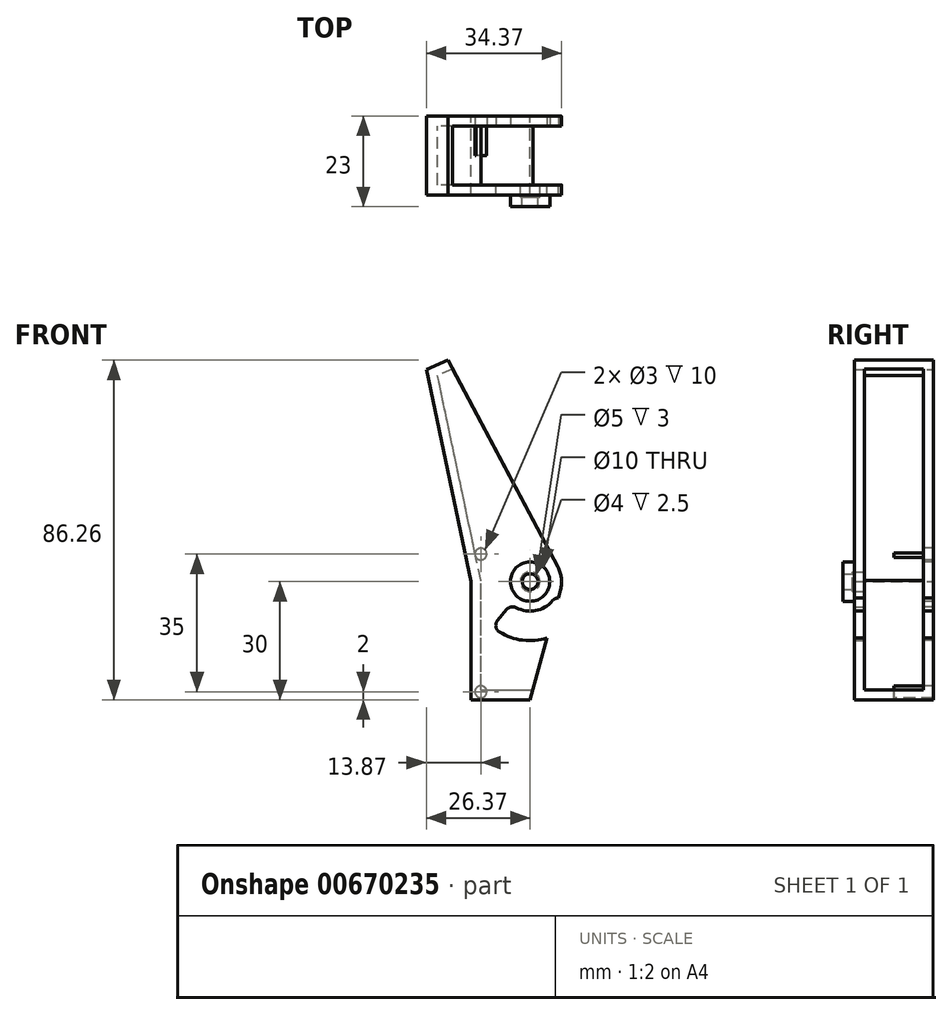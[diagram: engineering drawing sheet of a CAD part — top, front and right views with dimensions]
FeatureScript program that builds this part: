
annotation { "Feature Type Name" : "Feature", "Feature Type Description" : "" }
export const myFeature = defineFeature(function(context is Context, id is Id, definition is map)
    precondition{}
    {
        {
            var Q0;
            Q0=qCreatedBy(makeId("Front.planeOp"),FACE);
            var sketch = newSketch(context, id + "F0", { "sketchPlane" : qUnion([Q0])});
            skCircle(sketch, "E0", {"center": v(0, 0) * mm, "radius": 5 * mm});
            skSolve(sketch);
        }
        {
            var Q0;
            Q0=makeQuery(id+"F0.imprint","IMPRINT",FACE,{"disambiguationData":[TD([[makeQuery(id+"F0.imprint","IMPRINT",EDGE,{"derivedFrom":sQuery(id+"F0.wireOp",EDGE,"E0")}),1.0]])]});
            extrude(context, id + "F1", {"entities" : qUnion([Q0]), "depth" : 13 * mm, "offsetDistance" : 25 * mm});
        }
        {
            var Q0;
            Q0=qCreatedBy(makeId("Front.planeOp"),FACE);
            var sketch = newSketch(context, id + "F2", { "sketchPlane" : qUnion([Q0])});
            skLineSegment(sketch, "E1", {"start": v(7.06, 3.76) * mm, "end": v(-20.85, 56.26) * mm});
            skLineSegment(sketch, "E2", {"start": v(-20.85, 56.26) * mm, "end": v(-26.37, 53.9) * mm});
            skCircle(sketch, "E3", {"center": v(0, 0) * mm, "radius": 8 * mm});
            skCircle(sketch, "E4", {"center": v(0, 0) * mm, "radius": 60 * mm, "construction": true});
            skCircle(sketch, "E5", {"center": v(0, 0) * mm, "radius": 15 * mm, "construction": true});
            skLineSegment(sketch, "E6", {"start": v(-15, -30) * mm, "end": v(-15, 0) * mm});
            skLineSegment(sketch, "E7", {"start": v(-15, 0) * mm, "end": v(-26.37, 53.9) * mm});
            skLineSegment(sketch, "E8", {"start": v(0, -30) * mm, "end": v(7.71, -2.13) * mm});
            skLineSegment(sketch, "E9", {"start": v(-15, -30) * mm, "end": v(0, -30) * mm});
            skSolve(sketch);
        }
        {
            var Q0;
            {var subQ0=sQuery(id+"F2.wireOp",EDGE,"E2");Q0=makeQuery(id+"F2.imprint","IMPRINT",FACE,{"disambiguationData":[TD([[makeQuery(id+"F2.imprint","IMPRINT",EDGE,{"derivedFrom":subQ0}),1.0]])]});}
            var Q1;
            {var subQ0=sQuery(id+"F2.wireOp",EDGE,"E3");var subQ1=makeQuery(id+"F2.imprint","INTERSECT",VERTEX,{"derivedFrom":[sQuery(id+"F2.wireOp",EDGE,"ykASYGtx-wOTi-sknp-hqeL-7vM9FwBQ6DHq"),subQ0]});Q1=makeQuery(id+"F2.imprint","IMPRINT",FACE,{"disambiguationData":[TD([[makeQuery(id+"F2.imprint","IMPRINT",EDGE,{"disambiguationData":[TD([[subQ1,-1.0]])],"derivedFrom":subQ0}),1.0]])]});}
            var Q2;
            {var subQ4=sQuery(id+"F2.wireOp",EDGE,"AyMhzdsm-QS8C-DFPa-ot7w-gAMzFox847Q3");Q2=makeQuery(id+"F2.imprint","IMPRINT",FACE,{"disambiguationData":[TD([[makeQuery(id+"F2.imprint","IMPRINT",EDGE,{"derivedFrom":subQ4}),1.0]])]});}
            extrude(context, id + "F3", {"entities" : qUnion([Q0, Q1, Q2]), "operationType" : NewBodyOperationType.ADD, "endBound" : BoundingType.SYMMETRIC, "depth" : 20 * mm, "offsetDistance" : 25 * mm});
        }
        {
            var Q0;
            Q0=makeQuery(id+"F3.opExtrude","SWEPT_FACE",FACE,{"disambiguationData":[OSD([sQuery(id+"F2.wireOp",EDGE,"ykASYGtx-wOTi-sknp-hqeL-7vM9FwBQ6DHq")])]});
            var Q1;
            Q1=makeQuery(id+"F3.opExtrude","SWEPT_FACE",FACE,{"disambiguationData":[OSD([sQuery(id+"F2.wireOp",EDGE,"E3")])]});
            var Q2;
            Q2=makeQuery(id+"F3.opExtrude","SWEPT_FACE",FACE,{"disambiguationData":[OSD([sQuery(id+"F2.wireOp",EDGE,"E1")])]});
            var Q3;
            Q3=makeQuery(id+"F3.opExtrude","SWEPT_FACE",FACE,{"disambiguationData":[OSD([sQuery(id+"F2.wireOp",EDGE,"aPccT8il-h5co-UbTb-6sFN-h3AVFNnhd7PD")])]});
            var Q4;
            Q4=makeQuery(id+"F3.opExtrude","SWEPT_FACE",FACE,{"disambiguationData":[OSD([sQuery(id+"F2.wireOp",EDGE,"E8")])]});
            shell(context, id + "F4", {"entities" : qUnion([Q0, Q1, Q2, Q3, Q4]), "thickness" : 2.5 * mm});
        }
        {
            var Q0;
            Q0 = qSketchRegion(id + "F0", true);
            extrude(context, id + "F5", {"entities" : qUnion([Q0]), "operationType" : NewBodyOperationType.REMOVE, "oppositeDirection" : true, "depth" : 25 * mm, "offsetDistance" : 25 * mm});
        }
        {
            var Q0;
            Q0=qCreatedBy(makeId("Front.planeOp"),FACE);
            var sketch = newSketch(context, id + "F6", { "sketchPlane" : qUnion([Q0])});
            skCircle(sketch, "E10", {"center": v(-12.5, 7) * mm, "radius": 1.5 * mm});
            skCircle(sketch, "E11", {"center": v(-12.5, -28) * mm, "radius": 1.5 * mm});
            skCircle(sketch, "E12", {"center": v(0, 0) * mm, "radius": 7.5 * mm});
            skCircle(sketch, "E13", {"center": v(0, 0) * mm, "radius": 15 * mm});
            skLineSegment(sketch, "E14", {"start": v(-9.64, -11.5) * mm, "end": v(0, 0) * mm});
            skLineSegment(sketch, "E15", {"start": v(0, 0) * mm, "end": v(13, -7.5) * mm});
            skSolve(sketch);
        }
        {
            var Q0;
            {var subQ0=sQuery(id+"F6.wireOp",EDGE,"E14");var subQ1=sQuery(id+"F6.wireOp",EDGE,"E12");var subQ2=makeQuery(id+"F6.imprint","INTERSECT",VERTEX,{"derivedFrom":[subQ1,subQ0]});Q0=makeQuery(id+"F6.imprint","IMPRINT",FACE,{"disambiguationData":[TD([[makeQuery(id+"F6.imprint","IMPRINT",EDGE,{"disambiguationData":[TD([[subQ2,-1.0]])],"derivedFrom":subQ1}),-1.0]])]});}
            var Q1;
            Q1=makeQuery(id+"F6.imprint","IMPRINT",FACE,{"disambiguationData":[TD([[makeQuery(id+"F6.imprint","IMPRINT",EDGE,{"derivedFrom":sQuery(id+"F6.wireOp",EDGE,"E11")}),1.0]])]});
            var Q2;
            {var subQ0=sQuery(id+"F6.wireOp",EDGE,"E13");var subQ1=sQuery(id+"F6.wireOp",EDGE,"E10");var subQ2=makeQuery(id+"F6.imprint","INTERSECT",VERTEX,{"disambiguationData":[OD(0.0)],"derivedFrom":[subQ1,subQ0]});Q2=makeQuery(id+"F6.imprint","IMPRINT",FACE,{"disambiguationData":[TD([[makeQuery(id+"F6.imprint","IMPRINT",EDGE,{"disambiguationData":[TD([[subQ2,-1.0]])],"derivedFrom":subQ1}),1.0]])]});}
            var Q3;
            {var subQ0=sQuery(id+"F6.wireOp",EDGE,"E13");var subQ1=sQuery(id+"F6.wireOp",EDGE,"E10");var subQ2=makeQuery(id+"F6.imprint","INTERSECT",VERTEX,{"disambiguationData":[OD(0.0)],"derivedFrom":[subQ1,subQ0]});Q3=makeQuery(id+"F6.imprint","IMPRINT",FACE,{"disambiguationData":[TD([[makeQuery(id+"F6.imprint","IMPRINT",EDGE,{"disambiguationData":[TD([[subQ2,1.0]])],"derivedFrom":subQ1}),1.0]])]});}
            extrude(context, id + "F7", {"entities" : qUnion([Q0, Q1, Q2, Q3]), "operationType" : NewBodyOperationType.REMOVE, "oppositeDirection" : true, "depth" : 100 * mm, "offsetDistance" : 25 * mm});
        }
        {
            var Q0;
            {var subQ0=sQuery(id+"F6.wireOp",EDGE,"E14");var subQ1=sQuery(id+"F6.wireOp",EDGE,"E12");var subQ2=makeQuery(id+"F6.imprint","INTERSECT",VERTEX,{"derivedFrom":[subQ1,subQ0]});Q0=makeQuery(id+"F6.imprint","IMPRINT",FACE,{"disambiguationData":[TD([[makeQuery(id+"F6.imprint","IMPRINT",EDGE,{"disambiguationData":[TD([[subQ2,-1.0]])],"derivedFrom":subQ1}),-1.0]])]});}
            extrude(context, id + "F8", {"entities" : qUnion([Q0]), "operationType" : NewBodyOperationType.REMOVE, "depth" : 25 * mm, "offsetDistance" : 25 * mm});
        }
        {
            var Q0;
            Q0=makeQuery(id+"F7.boolean.opBoolean","COPY",EDGE,{"derivedFrom":makeQuery(id+"F7.opExtrude","SWEPT_EDGE",EDGE,{"disambiguationData":[OSD([sQuery(id+"F6.wireOp",EDGE,"E12"),sQuery(id+"F6.wireOp",EDGE,"E15")])]})});
            var Q1;
            Q1=makeQuery(id+"F7.boolean.opBoolean","COPY",EDGE,{"derivedFrom":makeQuery(id+"F7.opExtrude","SWEPT_EDGE",EDGE,{"disambiguationData":[OSD([sQuery(id+"F6.wireOp",EDGE,"E12"),sQuery(id+"F6.wireOp",EDGE,"E14")])]})});
            var Q2;
            Q2=makeQuery(id+"F7.boolean.opBoolean","COPY",EDGE,{"derivedFrom":makeQuery(id+"F7.opExtrude","SWEPT_EDGE",EDGE,{"disambiguationData":[OSD([sQuery(id+"F6.wireOp",EDGE,"E13"),sQuery(id+"F6.wireOp",EDGE,"E14")])]})});
            var Q3;
            Q3=makeQuery(id+"F7.boolean.opBoolean","COPY",EDGE,{"derivedFrom":makeQuery(id+"F7.opExtrude","SWEPT_EDGE",EDGE,{"disambiguationData":[OSD([sQuery(id+"F6.wireOp",EDGE,"E13"),sQuery(id+"F6.wireOp",EDGE,"E15")])]})});
            var Q4;
            Q4=makeQuery(id+"F8.boolean.opBoolean","COPY",EDGE,{"derivedFrom":makeQuery(id+"F8.opExtrude","SWEPT_EDGE",EDGE,{"disambiguationData":[OSD([sQuery(id+"F6.wireOp",EDGE,"E13"),sQuery(id+"F6.wireOp",EDGE,"E14")])]})});
            var Q5;
            Q5=makeQuery(id+"F8.boolean.opBoolean","COPY",EDGE,{"derivedFrom":makeQuery(id+"F8.opExtrude","SWEPT_EDGE",EDGE,{"disambiguationData":[OSD([sQuery(id+"F6.wireOp",EDGE,"E12"),sQuery(id+"F6.wireOp",EDGE,"E14")])]})});
            var Q6;
            Q6=makeQuery(id+"F8.boolean.opBoolean","COPY",EDGE,{"derivedFrom":makeQuery(id+"F8.opExtrude","SWEPT_EDGE",EDGE,{"disambiguationData":[OSD([sQuery(id+"F6.wireOp",EDGE,"E12"),sQuery(id+"F6.wireOp",EDGE,"E15")])]})});
            var Q7;
            Q7=makeQuery(id+"F8.boolean.opBoolean","COPY",EDGE,{"derivedFrom":makeQuery(id+"F8.opExtrude","SWEPT_EDGE",EDGE,{"disambiguationData":[OSD([sQuery(id+"F6.wireOp",EDGE,"E13"),sQuery(id+"F6.wireOp",EDGE,"E15")])]})});
            fillet(context, id + "F9", {"entities" : qUnion([Q0, Q1, Q2, Q3, Q4, Q5, Q6, Q7]), "radius" : 2 * mm, "tangentPropagation" : true, "allowEdgeOverflow" : false});
        }
        {
            var Q0;
            Q0=qCreatedBy(makeId("Front.planeOp"),FACE);
            var sketch = newSketch(context, id + "F10", { "sketchPlane" : qUnion([Q0])});
            skCircle(sketch, "E16", {"center": v(0, 0) * mm, "radius": 2 * mm});
            skSolve(sketch);
        }
        {
            var Q0;
            Q0 = qSketchRegion(id + "F10", true);
            extrude(context, id + "F11", {"entities" : qUnion([Q0]), "operationType" : NewBodyOperationType.REMOVE, "endBound" : BoundingType.SYMMETRIC, "depth" : 100 * mm, "offsetDistance" : 25 * mm});
        }
    });
